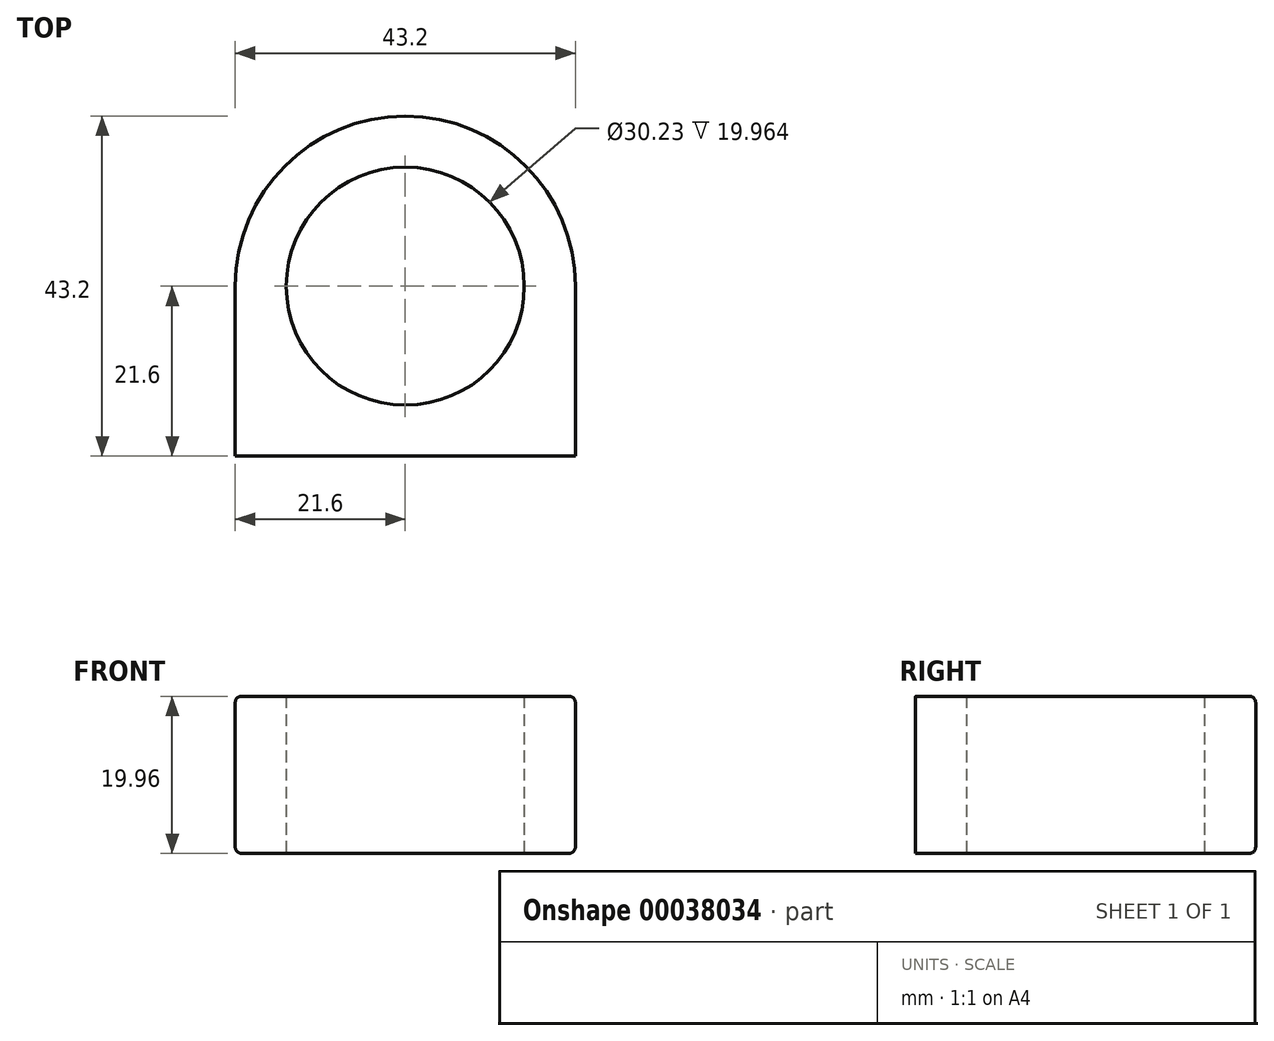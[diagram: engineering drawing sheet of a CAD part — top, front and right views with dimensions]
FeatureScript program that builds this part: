
annotation { "Feature Type Name" : "Feature", "Feature Type Description" : "" }
export const myFeature = defineFeature(function(context is Context, id is Id, definition is map)
    precondition{}
    {
        {
            var Q0;
            Q0=qCreatedBy(makeId("Top.planeOp"),FACE);
            var sketch = newSketch(context, id + "F0", { "sketchPlane" : qUnion([Q0])});
            skCircle(sketch, "E0", {"center": v(0, 0) * mm, "radius": 15.11 * mm});
            skCircle(sketch, "E1", {"center": v(0, 0) * mm, "radius": 21.6 * mm});
            skLineSegment(sketch, "E2.bottom", {"start": v(-21.6, 0) * mm, "end": v(21.6, 0) * mm});
            skLineSegment(sketch, "E2.top", {"start": v(-21.6, -21.6) * mm, "end": v(21.6, -21.6) * mm});
            skLineSegment(sketch, "E2.left", {"start": v(-21.6, 0) * mm, "end": v(-21.6, -21.6) * mm});
            skLineSegment(sketch, "E2.right", {"start": v(21.6, 0) * mm, "end": v(21.6, -21.6) * mm});
            skSolve(sketch);
        }
        {
            var Q0;
            Q0=qSketchRegion(id+"F0",true);
            extrude(context, id + "F1", {"entities" : qUnion([Q0]), "depth" : 19.96 * mm});
        }
        {
            var Q0;
            Q0=makeQuery(id+"F1.opExtrude","CAP_EDGE",EDGE,{"disambiguationData":[OSD([sQuery(id+"F0.wireOp",EDGE,"E1")])],"isStart":true});
            var Q1;
            Q1=makeQuery(id+"F1.opExtrude","CAP_EDGE",EDGE,{"disambiguationData":[OSD([sQuery(id+"F0.wireOp",EDGE,"E1")])],"isStart":false});
            fillet(context, id + "F2", {"entities" : qUnion([Q0, Q1]), "radius" : 0.8 * mm, "tangentPropagation" : true, "allowEdgeOverflow" : false});
        }
    });
